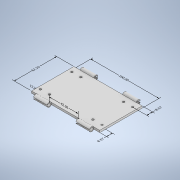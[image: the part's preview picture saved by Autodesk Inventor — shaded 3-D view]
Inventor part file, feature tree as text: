
AUTODESK INVENTOR PART (.ipt)
format: ipt  version: 2020 (Build 240168000, 168)  size: 278,016 bytes
history: native  units: mm
features: sketch x9, other x8, hole x8, extrude x6
ambient origin geometry x8: Origin, YZ Plane, XZ Plane, XY Plane, X Axis, Y Axis, Z Axis, Center Point
bodies: Solid1 (feature_tree)
feature tree (31):
  other  "Annotations"
  extrude  "Extrusion1"  Depth=62.1mm
  extrude  "Extrusion2"  Depth=42.1mm TaperAngle=0.0deg
  extrude  "Extrusion3"  Depth=0.001mm TaperAngle=0.0deg
  extrude  "Extrusion4"  Depth=8.95mm TaperAngle=0.0deg
  extrude  "Extrusion5"  Depth=100.0mm
  extrude  "Extrusion6"  Depth=100.0mm
  hole  "Hole5"  [1 undecoded]
  hole  "Hole6"  [1 undecoded]
  hole  "Hole7"  [1 undecoded]
  hole  "Hole8"  [1 undecoded]
  hole  "Hole10"  [1 undecoded]
  hole  "Hole9"  [1 undecoded]
  hole  "Hole12"  [1 undecoded]
  hole  "Hole11"  [1 undecoded]
  sketch  "Sketch1"  dims[d0=2.9mm d1=62.1mm]
  sketch  "Sketch4"  dims[d4=20.0mm d5=0.0mm d6=42.1mm d7=0.0mm]
  sketch  "Sketch9"  dims[d8=20.0mm d9=0.0mm d50=0.001mm d51=0.0mm]
  sketch  "Sketch14"  dims[d61=8.95mm d62=0.0mm d63=8.95mm d64=0.0mm]
  sketch  "Sketch15"  dims[d65=2.921mm d66=6.0mm d67=4.0mm d68=2.0mm d69=90.0deg d70=8.0mm d71=20.594885mm]
  sketch  "Sketch16"  dims[d84=2.921mm d85=6.0mm d86=4.0mm d87=2.0mm d88=90.0deg d89=8.0mm d90=20.594885mm]
  sketch  "Sketch17"  dims[d91=2.921mm d92=6.0mm d93=4.0mm d94=2.0mm d95=90.0deg d96=8.0mm d97=20.594885mm]
  sketch  "Sketch18"  dims[d98=2.921mm d99=6.0mm d100=4.0mm d101=2.0mm d102=90.0deg d103=8.0mm d104=20.594885mm]
  sketch  "Sketch19"  dims[d105=2.921mm d106=6.0mm d107=4.0mm d108=2.0mm d109=90.0deg d110=8.0mm d111=20.594885mm d112=2.921mm d113=6.0mm d114=4.0mm d115=2.0mm d116=90.0deg d117=8.0mm d118=20.594885mm d119=2.921mm d120=6.0mm d121=4.0mm d122=2.0mm d123=90.0deg d124=8.0mm d125=20.594885mm d126=2.921mm d127=6.0mm d128=4.0mm d129=2.0mm d130=90.0deg d131=8.0mm d132=20.594885mm d133=8.57mm d134=5.41mm d135=8.57mm d136=13.26mm d137=5.41mm d138=44.96mm d139=44.96mm d140=44.96mm d141=44.96mm d142=5.41mm d143=5.41mm d144=13.26mm d145=13.26mm d146=8.57mm d147=8.57mm d148=13.26mm d163=1.1mm d164=1.1mm d165=2.2mm d166=2.29907mm d167=3.3mm d168=3.3mm d171=6.062961mm d172=6.104896mm d174=6.063mm d176=1.1mm d177=1.1mm d178=2.2mm d150=13.26mm d151=44.947737mm d154=5.128261mm d155=8.57mm d180=5.063866mm d181=8.57mm d182=5.882722mm d183=5.186499mm d184=62.1mm d185=42.1mm d72=1.978463mm d73=6.235219mm d74=100.0mm]
  other  "Linear Dimension 6"
  other  "Linear Dimension 11"
  other  "Linear Dimension 12"
  other  "Linear Dimension 14"
  other  "Linear Dimension 15"
  other  "Linear Dimension 16"
  other  "Linear Dimension 17"
note: 8 required parameter values undecoded (feature->parameter linkage not recoverable at this tier; creation-order binding heuristic only, values carry confidence <= 0.55)
